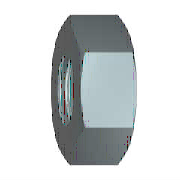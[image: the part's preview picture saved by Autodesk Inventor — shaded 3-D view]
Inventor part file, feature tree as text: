
AUTODESK INVENTOR PART (.ipt)
format: ipt  version: 2024 (Build 280153000, 153)  size: 171,008 bytes
history: native  units: mm (DEFAULTED — no unit token found)
features: chamfer x1, hole x1, other x1, plane x1
ambient origin geometry x7: Origin, YZ Plane, XZ Plane, X Axis, Y Axis, Z Axis, Center Point
bodies: Solid1 (feature_tree), Body (feature_tree)
feature tree (4):
  chamfer  "Chamfer1"  Distance=6.350853mm
  hole  "Thread"  [1 undecoded]
  other  "Work Axis1"
  plane  "Work Plane1"
note: 1 required parameter value undecoded (feature->parameter linkage not recoverable at this tier; creation-order binding heuristic only, values carry confidence <= 0.55)
